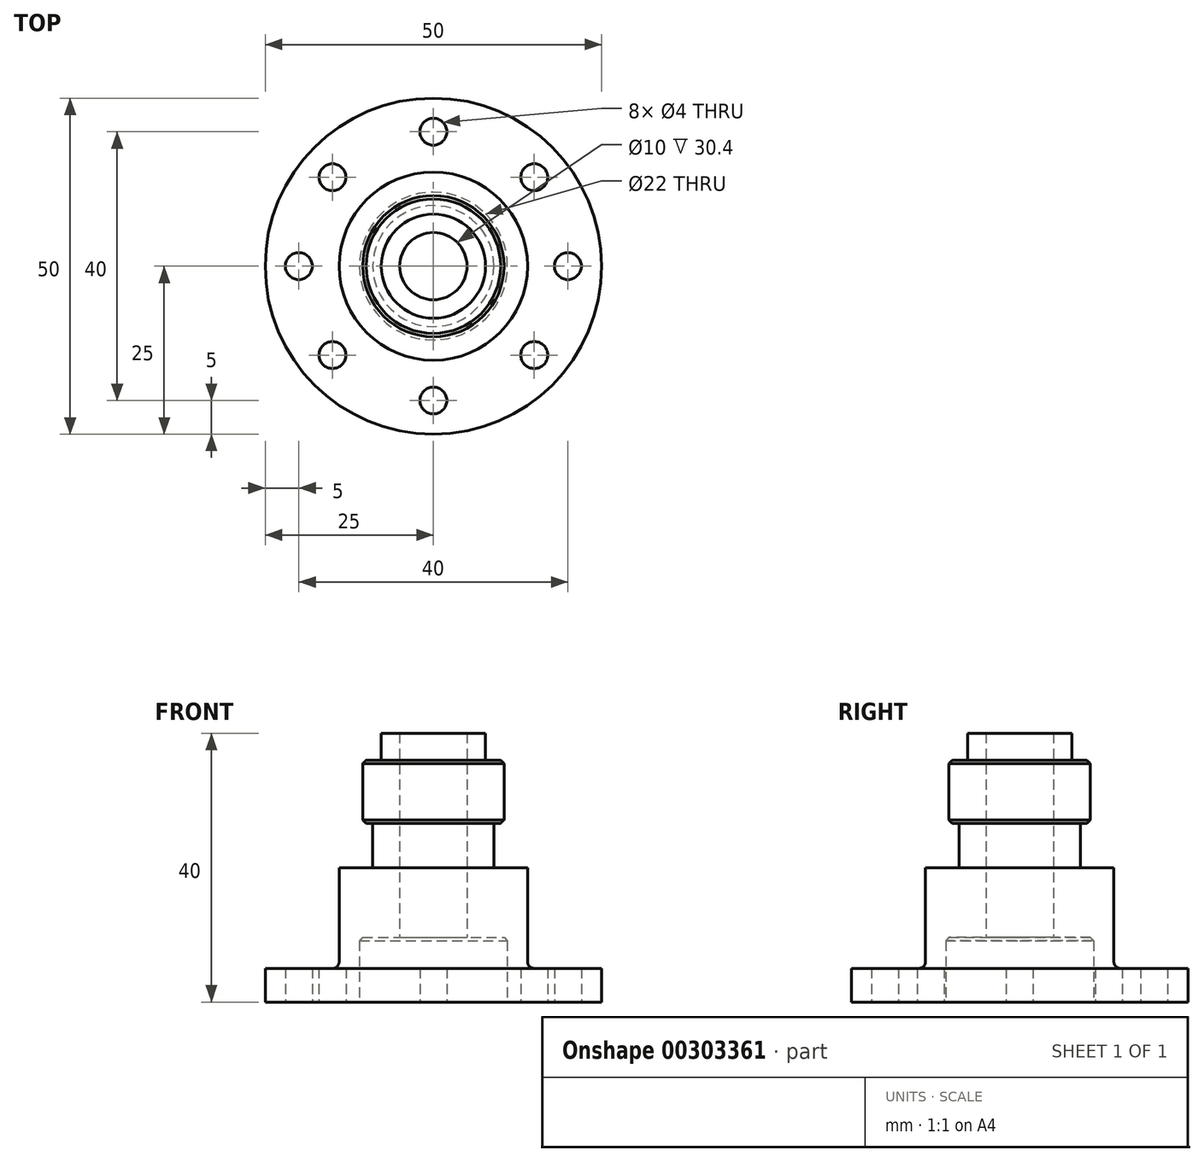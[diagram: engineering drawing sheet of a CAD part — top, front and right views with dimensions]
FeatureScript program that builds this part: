
annotation { "Feature Type Name" : "Feature", "Feature Type Description" : "" }
export const myFeature = defineFeature(function(context is Context, id is Id, definition is map)
    precondition{}
    {
        {
            var Q0;
            Q0=qCreatedBy(makeId("Front.planeOp"),FACE);
            var sketch = newSketch(context, id + "F0", { "sketchPlane" : qUnion([Q0])});
            skLineSegment(sketch, "E0", {"start": v(0, 0) * mm, "end": v(7.75, 0) * mm});
            skLineSegment(sketch, "E1", {"start": v(7.75, 0) * mm, "end": v(7.75, -4) * mm});
            skLineSegment(sketch, "E2", {"start": v(7.75, -4) * mm, "end": v(10.5, -4) * mm});
            skLineSegment(sketch, "E3", {"start": v(10.5, -4) * mm, "end": v(10.5, -13.4) * mm});
            skLineSegment(sketch, "E4", {"start": v(10.5, -13.4) * mm, "end": v(9, -13.4) * mm});
            skLineSegment(sketch, "E5", {"start": v(9, -13.4) * mm, "end": v(9, -20) * mm});
            skLineSegment(sketch, "E6", {"start": v(9, -20) * mm, "end": v(14, -20) * mm});
            skLineSegment(sketch, "E7", {"start": v(14, -20) * mm, "end": v(14, -34) * mm});
            skLineSegment(sketch, "E8", {"start": v(15, -35) * mm, "end": v(25, -35) * mm});
            skLineSegment(sketch, "E9", {"start": v(25, -35) * mm, "end": v(25, -40) * mm});
            skLineSegment(sketch, "E10", {"start": v(25, -40) * mm, "end": v(0, -40) * mm});
            skLineSegment(sketch, "E11", {"start": v(0, -40) * mm, "end": v(0, 0) * mm});
            skPoint(sketch, "E12.visualSharp", {"position": v(14, -35) * mm});
            skArc(sketch, "E12.filletArc", {"start": v(14, -34) * mm, "mid": v(14.3, -34.7) * mm, "end": v(15, -35) * mm});
            skSolve(sketch);
        }
        {
            var Q0;
            Q0 = qSketchRegion(id + "F0", true);
            var Q1;
            Q1=sQuery(id+"F0.wireOp",EDGE,"E11");
            revolve(context, id + "F1", {"entities" : qUnion([Q0]), "axis" : qUnion([Q1]), "revolveType" : RevolveType.FULL});
        }
        {
            var Q0;
            Q0=makeQuery(id+"F1.opRevolve","SWEPT_FACE",FACE,{"disambiguationData":[OSD([sQuery(id+"F0.wireOp",EDGE,"E10")])]});
            var sketch = newSketch(context, id + "F2", { "sketchPlane" : qUnion([Q0])});
            skCircle(sketch, "E13", {"center": v(0, 0) * mm, "radius": 20 * mm, "construction": true});
            skCircle(sketch, "E14", {"center": v(0, 0) * mm, "radius": 11 * mm});
            skCircle(sketch, "E15", {"center": v(0, 0) * mm, "radius": 5 * mm});
            skCircle(sketch, "E16", {"center": v(0, 20) * mm, "radius": 2 * mm});
            skCircle(sketch, "E17", {"center": v(0, -20) * mm, "radius": 2 * mm});
            skCircle(sketch, "E18", {"center": v(20, 0) * mm, "radius": 2 * mm});
            skCircle(sketch, "E19", {"center": v(-20, 0) * mm, "radius": 2 * mm});
            skCircle(sketch, "E20", {"center": v(15, 13.23) * mm, "radius": 2 * mm});
            skCircle(sketch, "E21", {"center": v(-15, 13.23) * mm, "radius": 2 * mm});
            skCircle(sketch, "E22", {"center": v(15, -13.23) * mm, "radius": 2 * mm});
            skCircle(sketch, "E23", {"center": v(-15, -13.23) * mm, "radius": 2 * mm});
            skSolve(sketch);
        }
        {
            var Q0;
            Q0=makeQuery(id+"F2.imprint","IMPRINT",FACE,{"disambiguationData":[TD([[makeQuery(id+"F2.imprint","IMPRINT",EDGE,{"derivedFrom":sQuery(id+"F2.wireOp",EDGE,"E15")}),1.0]])]});
            extrude(context, id + "F3", {"entities" : qUnion([Q0]), "operationType" : NewBodyOperationType.REMOVE, "oppositeDirection" : true, "depth" : 40 * mm});
        }
        {
            var Q0;
            Q0=makeQuery(id+"F2.imprint","IMPRINT",FACE,{"disambiguationData":[TD([[makeQuery(id+"F2.imprint","IMPRINT",EDGE,{"derivedFrom":sQuery(id+"F2.wireOp",EDGE,"E14")}),1.0]])]});
            var Q1;
            Q1=makeQuery(id+"F2.imprint","IMPRINT",FACE,{"disambiguationData":[TD([[makeQuery(id+"F2.imprint","IMPRINT",EDGE,{"derivedFrom":sQuery(id+"F2.wireOp",EDGE,"0fk2jcBL-R3u0-Eb3q-jmo1-aC3HYsmPUFzK")}),1.0]])]});
            extrude(context, id + "F4", {"entities" : qUnion([Q0, Q1]), "operationType" : NewBodyOperationType.REMOVE, "oppositeDirection" : true, "depth" : 9.6 * mm});
        }
        {
            var Q0;
            Q0=makeQuery(id+"F2.imprint","IMPRINT",FACE,{"disambiguationData":[TD([[makeQuery(id+"F2.imprint","IMPRINT",EDGE,{"derivedFrom":sQuery(id+"F2.wireOp",EDGE,"E20")}),1.0]])]});
            var Q1;
            Q1=makeQuery(id+"F2.imprint","IMPRINT",FACE,{"disambiguationData":[TD([[makeQuery(id+"F2.imprint","IMPRINT",EDGE,{"derivedFrom":sQuery(id+"F2.wireOp",EDGE,"E21")}),1.0]])]});
            var Q2;
            Q2=makeQuery(id+"F2.imprint","IMPRINT",FACE,{"disambiguationData":[TD([[makeQuery(id+"F2.imprint","IMPRINT",EDGE,{"derivedFrom":sQuery(id+"F2.wireOp",EDGE,"E23")}),1.0]])]});
            var Q3;
            Q3=makeQuery(id+"F2.imprint","IMPRINT",FACE,{"disambiguationData":[TD([[makeQuery(id+"F2.imprint","IMPRINT",EDGE,{"derivedFrom":sQuery(id+"F2.wireOp",EDGE,"E22")}),1.0]])]});
            var Q4;
            Q4=makeQuery(id+"F2.imprint","IMPRINT",FACE,{"disambiguationData":[TD([[makeQuery(id+"F2.imprint","IMPRINT",EDGE,{"derivedFrom":sQuery(id+"F2.wireOp",EDGE,"E17")}),1.0]])]});
            var Q5;
            Q5=makeQuery(id+"F2.imprint","IMPRINT",FACE,{"disambiguationData":[TD([[makeQuery(id+"F2.imprint","IMPRINT",EDGE,{"derivedFrom":sQuery(id+"F2.wireOp",EDGE,"E18")}),1.0]])]});
            var Q6;
            Q6=makeQuery(id+"F2.imprint","IMPRINT",FACE,{"disambiguationData":[TD([[makeQuery(id+"F2.imprint","IMPRINT",EDGE,{"derivedFrom":sQuery(id+"F2.wireOp",EDGE,"E19")}),1.0]])]});
            var Q7;
            Q7=makeQuery(id+"F2.imprint","IMPRINT",FACE,{"disambiguationData":[TD([[makeQuery(id+"F2.imprint","IMPRINT",EDGE,{"derivedFrom":sQuery(id+"F2.wireOp",EDGE,"E16")}),1.0]])]});
            extrude(context, id + "F5", {"entities" : qUnion([Q0, Q1, Q2, Q3, Q4, Q5, Q6, Q7]), "operationType" : NewBodyOperationType.REMOVE, "oppositeDirection" : true, "depth" : 5 * mm});
        }
        {
            var Q0;
            Q0=makeQuery(id+"F4.boolean.opBoolean","COPY",EDGE,{"derivedFrom":makeQuery(id+"F4.opExtrude","CAP_EDGE",EDGE,{"disambiguationData":[OSD([sQuery(id+"F2.wireOp",EDGE,"E14")])],"isStart":false})});
            chamfer(context, id + "F6", {"entities" : qUnion([Q0]), "width" : .5 * mm, "tangentPropagation" : true});
        }
        {
            var Q0;
            Q0=makeQuery(id+"F1.opRevolve","SWEPT_EDGE",EDGE,{"disambiguationData":[OSD([sQuery(id+"F0.wireOp",EDGE,"E3"),sQuery(id+"F0.wireOp",EDGE,"E4")])]});
            chamfer(context, id + "F7", {"entities" : qUnion([Q0]), "chamferType" : ChamferType.OFFSET_ANGLE, "width" : .5 * mm, "oppositeDirection" : false, "angle" : 45 * degree, "tangentPropagation" : true});
        }
        {
            var Q0;
            Q0=makeQuery(id+"F1.opRevolve","SWEPT_EDGE",EDGE,{"disambiguationData":[OSD([sQuery(id+"F0.wireOp",EDGE,"E2"),sQuery(id+"F0.wireOp",EDGE,"E3")])]});
            chamfer(context, id + "F8", {"entities" : qUnion([Q0]), "chamferType" : ChamferType.OFFSET_ANGLE, "width" : .5 * mm, "oppositeDirection" : false, "angle" : 45 * degree, "tangentPropagation" : true});
        }
    });
